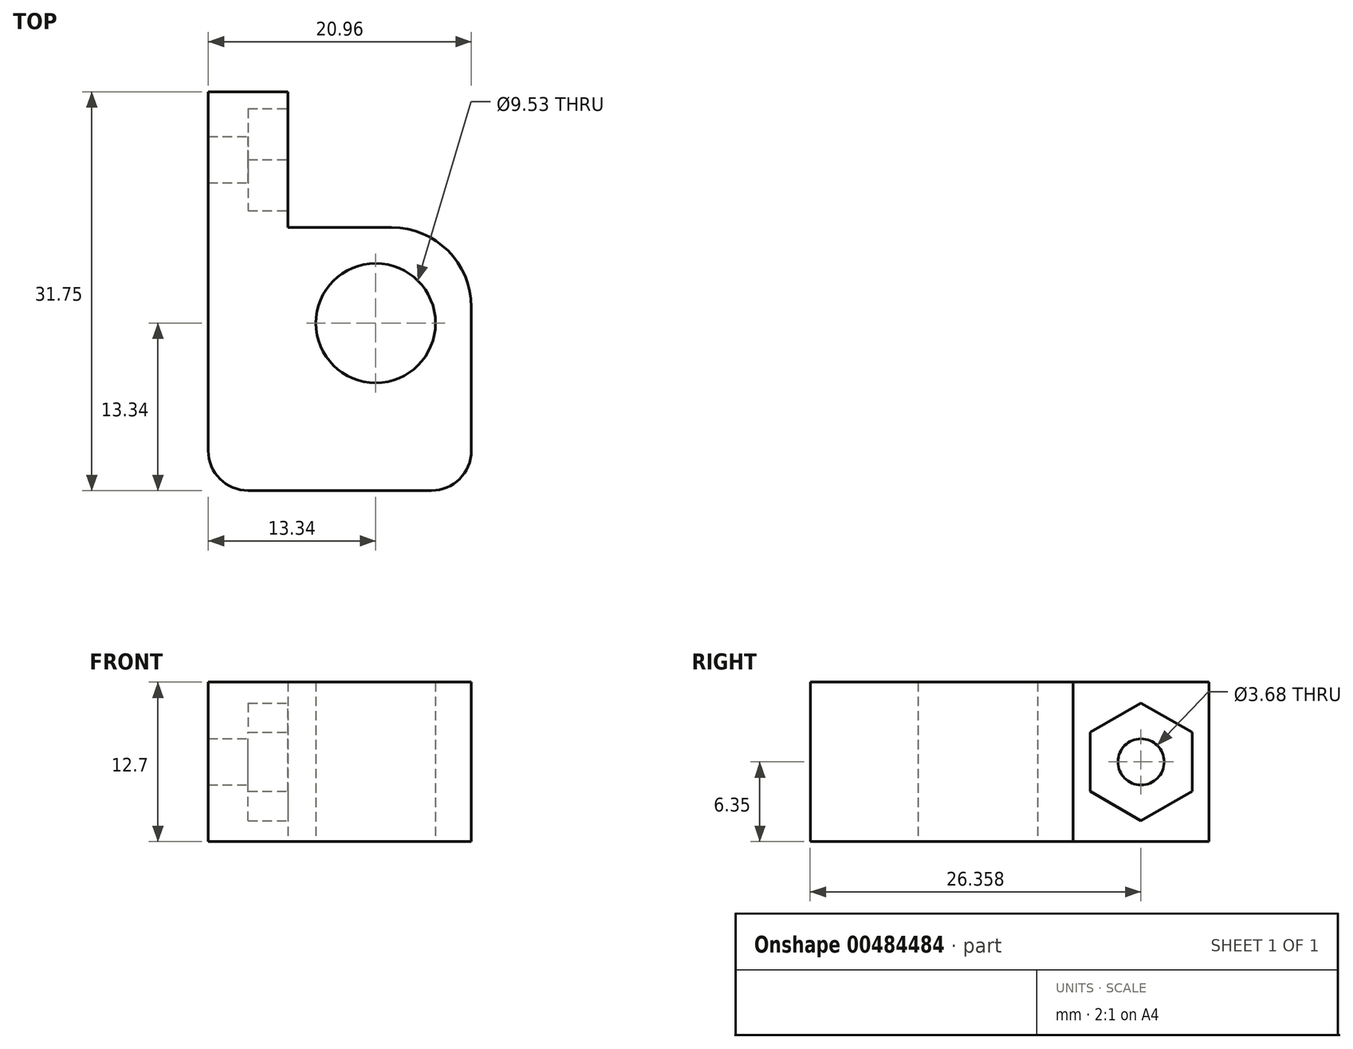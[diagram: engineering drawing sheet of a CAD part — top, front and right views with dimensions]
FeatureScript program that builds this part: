
annotation { "Feature Type Name" : "Feature", "Feature Type Description" : "" }
export const myFeature = defineFeature(function(context is Context, id is Id, definition is map)
    precondition{}
    {
        {
            var Q0;
            Q0=qCreatedBy(makeId("Top.planeOp"),FACE);
            var sketch = newSketch(context, id + "F0", { "sketchPlane" : qUnion([Q0])});
            skCircle(sketch, "E0", {"center": v(0, 0) * mm, "radius": 4.76 * mm});
            skLineSegment(sketch, "E1", {"start": v(-13.33, -13.34) * mm, "end": v(18.41, -13.34) * mm});
            skLineSegment(sketch, "E2", {"start": v(18.41, -13.34) * mm, "end": v(18.41, -6.99) * mm});
            skLineSegment(sketch, "E3", {"start": v(18.41, -6.98) * mm, "end": v(7.62, -6.99) * mm});
            skLineSegment(sketch, "E4", {"start": v(7.62, -6.99) * mm, "end": v(7.62, 7.62) * mm});
            skLineSegment(sketch, "E5", {"start": v(7.62, 7.62) * mm, "end": v(-6.99, 7.62) * mm});
            skLineSegment(sketch, "E6", {"start": v(-6.99, 7.62) * mm, "end": v(-6.99, 18.41) * mm});
            skLineSegment(sketch, "E7", {"start": v(-6.99, 18.41) * mm, "end": v(-13.34, 18.41) * mm});
            skLineSegment(sketch, "E8", {"start": v(-13.34, 18.41) * mm, "end": v(-13.33, -13.34) * mm});
            skSolve(sketch);
        }
        {
            var Q0;
            Q0=qSketchRegion(id+"F0",true);
            extrude(context, id + "F1", {"entities" : qUnion([Q0]), "depth" : 12.7 * mm, "offsetDistance" : 25.4 * mm});
        }
        {
            var Q0;
            Q0=makeQuery(id+"F1.opExtrude","SWEPT_EDGE",EDGE,{"disambiguationData":[OSD([sQuery(id+"F0.wireOp",EDGE,"E4"),sQuery(id+"F0.wireOp",EDGE,"E5")])]});
            fillet(context, id + "F2", {"entities" : qUnion([Q0]), "radius" : 6.35 * mm, "tangentPropagation" : true, "allowEdgeOverflow" : false});
        }
        {
            var Q0;
            Q0=makeQuery(id+"F1.opExtrude","SWEPT_EDGE",EDGE,{"disambiguationData":[OSD([sQuery(id+"F0.wireOp",EDGE,"E1"),sQuery(id+"F0.wireOp",EDGE,"E8")])]});
            fillet(context, id + "F3", {"entities" : qUnion([Q0]), "radius" : 3.17 * mm, "tangentPropagation" : true, "allowEdgeOverflow" : false});
        }
        {
            var Q0;
            Q0=makeQuery(id+"F1.opExtrude","SWEPT_FACE",FACE,{"disambiguationData":[OSD([sQuery(id+"F0.wireOp",EDGE,"E3")])]});
            var sketch = newSketch(context, id + "F4", { "sketchPlane" : qUnion([Q0])});
            skCircle(sketch, "E9", {"center": v(-13.02, 6.35) * mm, "radius": 1.84 * mm});
            skPoint(sketch, "E9.centerSnap0", {"position": v(-18.41, 6.35) * mm});
            skPoint(sketch, "E9.centerSnap1", {"position": v(-13.02, 0) * mm});
            skSolve(sketch);
        }
        {
            var Q0;
            Q0=qSketchRegion(id+"F4",true);
            extrude(context, id + "F5", {"entities" : qUnion([Q0]), "operationType" : NewBodyOperationType.REMOVE, "oppositeDirection" : true, "depth" : 25.4 * mm, "offsetDistance" : 25.4 * mm});
        }
        {
            var Q0;
            Q0=makeQuery(id+"F1.opExtrude","SWEPT_FACE",FACE,{"disambiguationData":[OSD([sQuery(id+"F0.wireOp",EDGE,"E3")])]});
            var sketch = newSketch(context, id + "F6", { "sketchPlane" : qUnion([Q0])});
            skCircle(sketch, "E10.cCircle", {"center": v(-13.02, 6.35) * mm, "radius": 4.06 * mm, "construction": true});
            skLineSegment(sketch, "E10.0", {"start": v(-13.02, 1.66) * mm, "end": v(-17.08, 4) * mm});
            skLineSegment(sketch, "E10.1", {"start": v(-17.08, 4) * mm, "end": v(-17.08, 8.7) * mm});
            skLineSegment(sketch, "E10.2", {"start": v(-17.08, 8.7) * mm, "end": v(-13.02, 11.04) * mm});
            skLineSegment(sketch, "E10.3", {"start": v(-13.02, 11.04) * mm, "end": v(-8.95, 8.7) * mm});
            skLineSegment(sketch, "E10.4", {"start": v(-8.95, 8.7) * mm, "end": v(-8.95, 4) * mm});
            skLineSegment(sketch, "E10.5", {"start": v(-8.95, 4) * mm, "end": v(-13.02, 1.66) * mm});
            skPoint(sketch, "E10.0.midPoint", {"position": v(-15.05, 2.83) * mm});
            skSolve(sketch);
        }
        {
            var Q0;
            Q0=qSketchRegion(id+"F6",true);
            extrude(context, id + "F7", {"entities" : qUnion([Q0]), "operationType" : NewBodyOperationType.REMOVE, "oppositeDirection" : true, "depth" : 3.17 * mm, "offsetDistance" : 25.4 * mm});
        }
        {
            var Q0;
            Q0=makeQuery(id+"F1.opExtrude","SWEPT_FACE",FACE,{"disambiguationData":[OSD([sQuery(id+"F0.wireOp",EDGE,"E6")])]});
            var sketch = newSketch(context, id + "F8", { "sketchPlane" : qUnion([Q0])});
            skCircle(sketch, "E11", {"center": v(13.02, 6.35) * mm, "radius": 1.84 * mm});
            skPoint(sketch, "E11.centerSnap0", {"position": v(13.02, 12.7) * mm});
            skPoint(sketch, "E11.centerSnap1", {"position": v(18.41, 6.35) * mm});
            skSolve(sketch);
        }
        {
            var Q0;
            Q0=qSketchRegion(id+"F8",true);
            extrude(context, id + "F9", {"entities" : qUnion([Q0]), "operationType" : NewBodyOperationType.REMOVE, "oppositeDirection" : true, "depth" : 25.4 * mm, "offsetDistance" : 25.4 * mm});
        }
        {
            var Q0;
            Q0=makeQuery(id+"F1.opExtrude","SWEPT_FACE",FACE,{"disambiguationData":[OSD([sQuery(id+"F0.wireOp",EDGE,"E6")])]});
            var sketch = newSketch(context, id + "F10", { "sketchPlane" : qUnion([Q0])});
            skCircle(sketch, "E12.cCircle", {"center": v(13.02, 6.35) * mm, "radius": 4.06 * mm, "construction": true});
            skLineSegment(sketch, "E12.0", {"start": v(8.95, 4) * mm, "end": v(8.95, 8.7) * mm});
            skLineSegment(sketch, "E12.1", {"start": v(8.95, 8.7) * mm, "end": v(13.02, 11.04) * mm});
            skLineSegment(sketch, "E12.2", {"start": v(13.02, 11.04) * mm, "end": v(17.08, 8.7) * mm});
            skLineSegment(sketch, "E12.3", {"start": v(17.08, 8.7) * mm, "end": v(17.08, 4) * mm});
            skLineSegment(sketch, "E12.4", {"start": v(17.08, 4) * mm, "end": v(13.02, 1.66) * mm});
            skLineSegment(sketch, "E12.5", {"start": v(13.02, 1.66) * mm, "end": v(8.95, 4) * mm});
            skPoint(sketch, "E12.0.midPoint", {"position": v(8.95, 6.35) * mm});
            skSolve(sketch);
        }
        {
            var Q0;
            Q0=qSketchRegion(id+"F10",true);
            extrude(context, id + "F11", {"entities" : qUnion([Q0]), "operationType" : NewBodyOperationType.REMOVE, "oppositeDirection" : true, "depth" : 3.17 * mm, "offsetDistance" : 25.4 * mm});
        }
        {
            var Q0;
            Q0=makeQuery(id+"F1.opExtrude","CAP_FACE",FACE,{"disambiguationData":[OSD([sQuery(id+"F0.wireOp",EDGE,"E0"),sQuery(id+"F0.wireOp",EDGE,"E1"),sQuery(id+"F0.wireOp",EDGE,"E2"),sQuery(id+"F0.wireOp",EDGE,"E3"),sQuery(id+"F0.wireOp",EDGE,"E4"),sQuery(id+"F0.wireOp",EDGE,"E5"),sQuery(id+"F0.wireOp",EDGE,"E6"),sQuery(id+"F0.wireOp",EDGE,"E7"),sQuery(id+"F0.wireOp",EDGE,"E8")])],"isStart":false});
            var sketch = newSketch(context, id + "F12", { "sketchPlane" : qUnion([Q0])});
            skLineSegment(sketch, "E13.bottom", {"start": v(28.24, -21.2) * mm, "end": v(7.62, -21.2) * mm});
            skLineSegment(sketch, "E13.top", {"start": v(28.24, 8.53) * mm, "end": v(7.62, 8.53) * mm});
            skLineSegment(sketch, "E13.left", {"start": v(28.24, -21.2) * mm, "end": v(28.24, 8.53) * mm});
            skLineSegment(sketch, "E13.right", {"start": v(7.62, -21.2) * mm, "end": v(7.62, 8.53) * mm});
            skSolve(sketch);
        }
        {
            var Q0;
            Q0 = qSketchRegion(id + "F12", true);
            extrude(context, id + "F13", {"entities" : qUnion([Q0]), "operationType" : NewBodyOperationType.REMOVE, "oppositeDirection" : true, "depth" : 25.4 * mm, "offsetDistance" : 25.4 * mm});
        }
        {
            var Q0;
            Q0=makeQuery(id+"F13.boolean.opBoolean","INTERSECT",EDGE,{"derivedFrom":[makeQuery(id+"F1.opExtrude","SWEPT_FACE",FACE,{"disambiguationData":[OSD([sQuery(id+"F0.wireOp",EDGE,"E1")])]}),makeQuery(id+"F13.opExtrude","SWEPT_FACE",FACE,{"disambiguationData":[OSD([sQuery(id+"F12.wireOp",EDGE,"E13.right")])]})]});
            fillet(context, id + "F14", {"entities" : qUnion([Q0]), "radius" : 3.17 * mm, "tangentPropagation" : true, "allowEdgeOverflow" : false});
        }
    });
